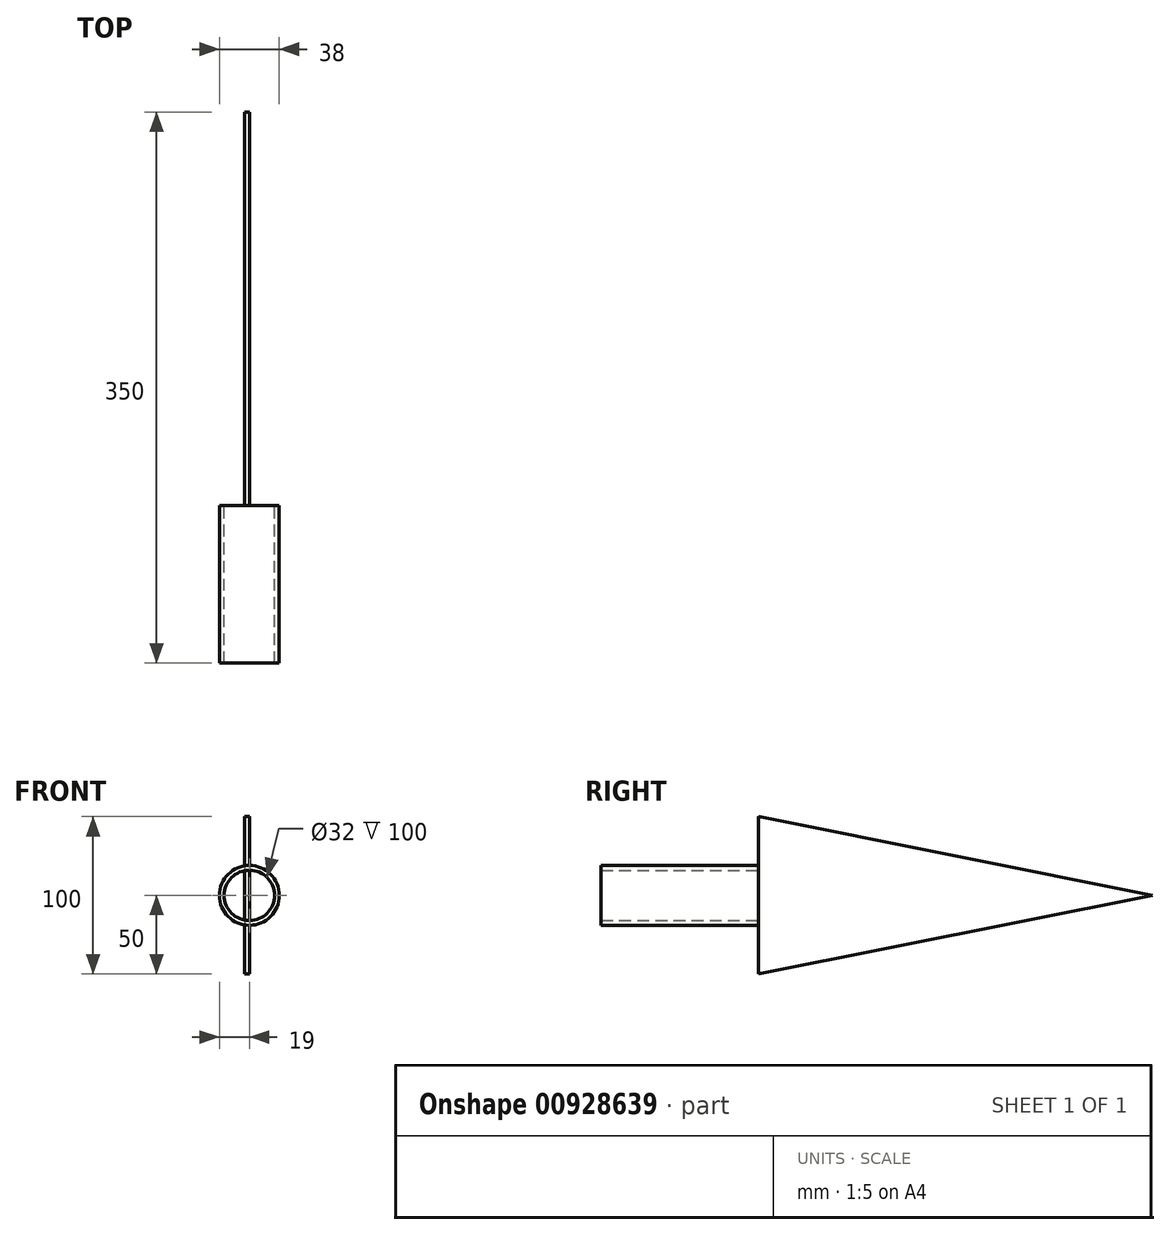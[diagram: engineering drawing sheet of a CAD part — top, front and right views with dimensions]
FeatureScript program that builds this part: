
annotation { "Feature Type Name" : "Feature", "Feature Type Description" : "" }
export const myFeature = defineFeature(function(context is Context, id is Id, definition is map)
    precondition{}
    {
        {
            var Q0;
            Q0=qCreatedBy(makeId("Front.planeOp"),FACE);
            var sketch = newSketch(context, id + "F0", { "sketchPlane" : qUnion([Q0])});
            skCircle(sketch, "E0", {"center": v(0, 0) * mm, "radius": 19 * mm});
            skCircle(sketch, "E1", {"center": v(0, 0) * mm, "radius": 16 * mm});
            skSolve(sketch);
        }
        {
            var Q0;
            Q0=makeQuery(id+"F0.imprint","IMPRINT",FACE,{"disambiguationData":[TD([[makeQuery(id+"F0.imprint","IMPRINT",EDGE,{"derivedFrom":sQuery(id+"F0.wireOp",EDGE,"E0")}),1.0]])]});
            extrude(context, id + "F1", {"entities" : qUnion([Q0]), "depth" : 100 * mm, "offsetDistance" : 25 * mm});
        }
        {
            var Q0;
            Q0=qCreatedBy(makeId("Right.planeOp"),FACE);
            var sketch = newSketch(context, id + "F2", { "sketchPlane" : qUnion([Q0])});
            skLineSegment(sketch, "E2", {"start": v(250, 0) * mm, "end": v(0, -50) * mm});
            skLineSegment(sketch, "E3", {"start": v(0, -50) * mm, "end": v(0, 0) * mm});
            skLineSegment(sketch, "E4", {"start": v(250, 0) * mm, "end": v(0, 50) * mm});
            skLineSegment(sketch, "E5", {"start": v(0, 50) * mm, "end": v(0, 0) * mm});
            skSolve(sketch);
        }
        {
            var Q0;
            Q0 = qSketchRegion(id + "F2", true);
            extrude(context, id + "F3", {"entities" : qUnion([Q0]), "operationType" : NewBodyOperationType.ADD, "oppositeDirection" : true, "depth" : 3 * mm, "offsetDistance" : 25 * mm});
        }
    });
